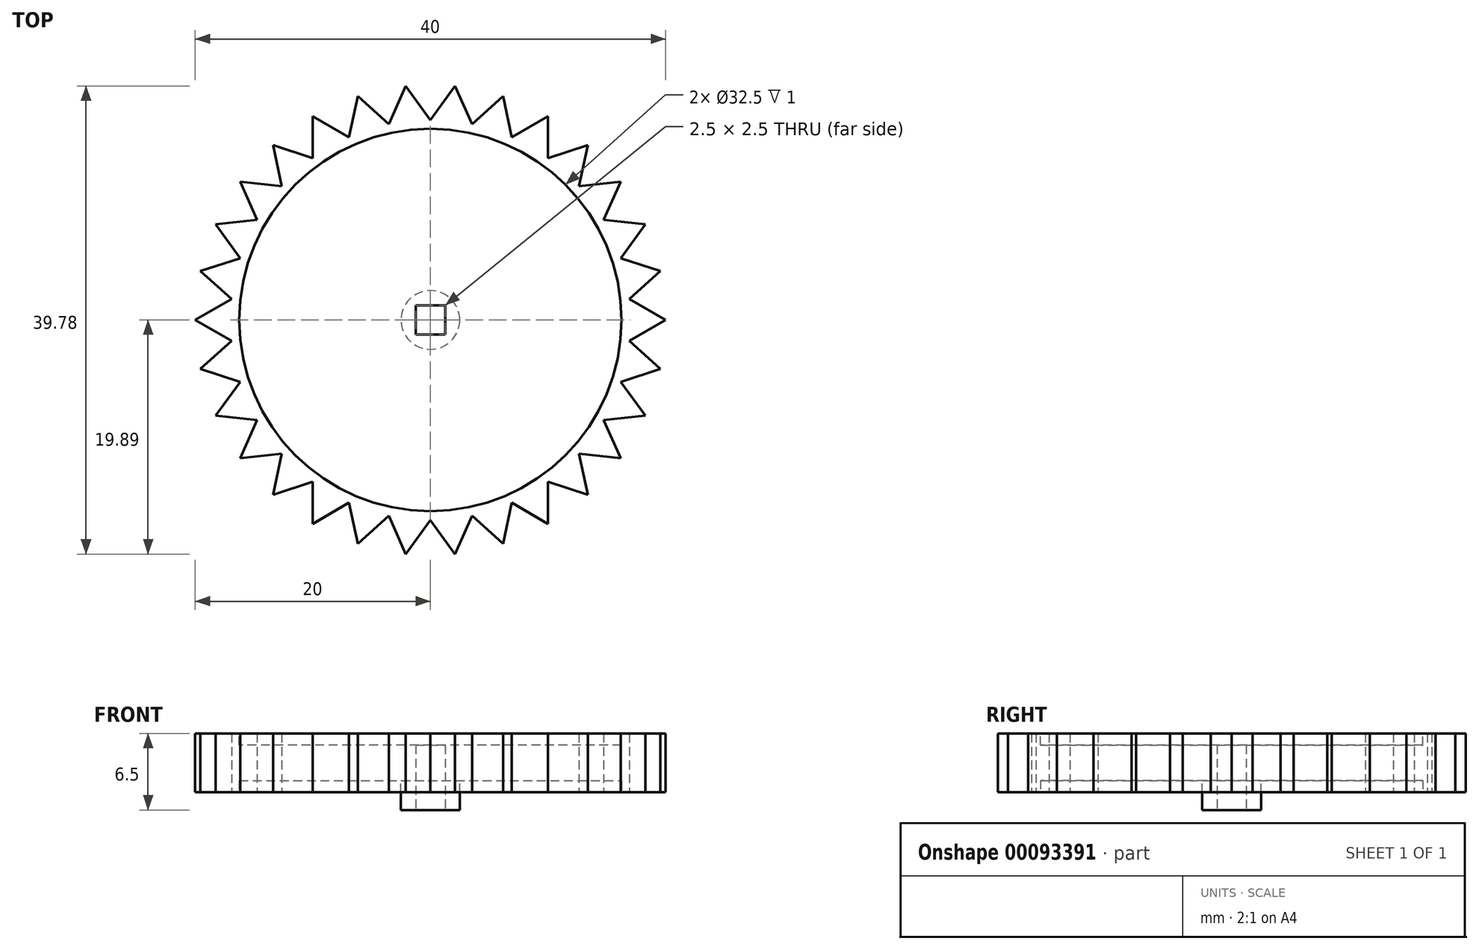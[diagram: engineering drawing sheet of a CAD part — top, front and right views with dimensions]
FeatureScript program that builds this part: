
annotation { "Feature Type Name" : "Feature", "Feature Type Description" : "" }
export const myFeature = defineFeature(function(context is Context, id is Id, definition is map)
    precondition{}
    {
        {
            var Q0;
            Q0=qCreatedBy(makeId("Top.planeOp"),FACE);
            var sketch = newSketch(context, id + "F0", { "sketchPlane" : qUnion([Q0])});
            skCircle(sketch, "E0", {"center": v(0, 0) * mm, "radius": 20 * mm});
            skLineSegment(sketch, "E1", {"start": v(0, 0) * mm, "end": v(-2.1, -19.9) * mm, "construction": true});
            skLineSegment(sketch, "E2", {"start": v(0, 0) * mm, "end": v(2.1, -19.9) * mm, "construction": true});
            skLineSegment(sketch, "E3", {"start": v(-2.1, -19.9) * mm, "end": v(0, -17) * mm});
            skLineSegment(sketch, "E4", {"start": v(0, -17) * mm, "end": v(2.1, -19.9) * mm});
            skArc(sketch, "E5", {"start": v(-2.1, -19.9) * mm, "mid": v(0, -20) * mm, "end": v(2.1, -19.9) * mm});
            skLineSegment(sketch, "E6.1.0", {"start": v(2.1, -19.9) * mm, "end": v(3.54, -16.63) * mm});
            skLineSegment(sketch, "E6.1.1", {"start": v(3.54, -16.63) * mm, "end": v(6.18, -19.02) * mm});
            skArc(sketch, "E6.1.2", {"start": v(2.1, -19.9) * mm, "mid": v(4.16, -19.56) * mm, "end": v(6.18, -19.02) * mm});
            skLineSegment(sketch, "E6.2.0", {"start": v(6.18, -19.02) * mm, "end": v(6.92, -15.53) * mm});
            skLineSegment(sketch, "E6.2.1", {"start": v(6.92, -15.53) * mm, "end": v(10, -17.32) * mm});
            skArc(sketch, "E6.2.2", {"start": v(6.18, -19.02) * mm, "mid": v(8.13, -18.27) * mm, "end": v(10, -17.32) * mm});
            skLineSegment(sketch, "E7.1.3.0", {"start": v(10, -17.32) * mm, "end": v(10, -13.76) * mm});
            skLineSegment(sketch, "E7.3.3.0", {"start": v(10, -13.76) * mm, "end": v(13.38, -14.86) * mm});
            skArc(sketch, "E7.6.3.0", {"start": v(10, -17.32) * mm, "mid": v(11.76, -16.18) * mm, "end": v(13.38, -14.86) * mm});
            skLineSegment(sketch, "E7.1.4.0", {"start": v(13.38, -14.86) * mm, "end": v(12.64, -11.38) * mm});
            skLineSegment(sketch, "E7.3.4.0", {"start": v(12.64, -11.38) * mm, "end": v(16.18, -11.76) * mm});
            skArc(sketch, "E7.6.4.0", {"start": v(13.38, -14.86) * mm, "mid": v(14.86, -13.38) * mm, "end": v(16.18, -11.76) * mm});
            skLineSegment(sketch, "E7.1.5.0", {"start": v(16.18, -11.76) * mm, "end": v(14.73, -8.5) * mm});
            skLineSegment(sketch, "E7.3.5.0", {"start": v(14.73, -8.5) * mm, "end": v(18.27, -8.13) * mm});
            skArc(sketch, "E7.6.5.0", {"start": v(16.18, -11.76) * mm, "mid": v(17.32, -10) * mm, "end": v(18.27, -8.13) * mm});
            skLineSegment(sketch, "E7.1.6.0", {"start": v(18.27, -8.13) * mm, "end": v(16.17, -5.25) * mm});
            skLineSegment(sketch, "E7.3.6.0", {"start": v(16.17, -5.25) * mm, "end": v(19.56, -4.16) * mm});
            skArc(sketch, "E7.6.6.0", {"start": v(18.27, -8.13) * mm, "mid": v(19.02, -6.18) * mm, "end": v(19.56, -4.16) * mm});
            skLineSegment(sketch, "E7.1.7.0", {"start": v(19.56, -4.16) * mm, "end": v(16.91, -1.78) * mm});
            skLineSegment(sketch, "E7.3.7.0", {"start": v(16.91, -1.78) * mm, "end": v(20, 0) * mm});
            skArc(sketch, "E7.6.7.0", {"start": v(19.56, -4.16) * mm, "mid": v(19.9, -2.1) * mm, "end": v(20, 0) * mm});
            skLineSegment(sketch, "E7.1.8.0", {"start": v(20, 0) * mm, "end": v(16.91, 1.78) * mm});
            skLineSegment(sketch, "E7.3.8.0", {"start": v(16.91, 1.78) * mm, "end": v(19.56, 4.16) * mm});
            skArc(sketch, "E7.6.8.0", {"start": v(20, 0) * mm, "mid": v(19.9, 2.1) * mm, "end": v(19.56, 4.16) * mm});
            skLineSegment(sketch, "E7.1.9.0", {"start": v(19.56, 4.16) * mm, "end": v(16.17, 5.25) * mm});
            skLineSegment(sketch, "E7.3.9.0", {"start": v(16.17, 5.25) * mm, "end": v(18.27, 8.13) * mm});
            skArc(sketch, "E7.6.9.0", {"start": v(19.56, 4.16) * mm, "mid": v(19.02, 6.18) * mm, "end": v(18.27, 8.13) * mm});
            skLineSegment(sketch, "E7.1.10.0", {"start": v(18.27, 8.13) * mm, "end": v(14.73, 8.5) * mm});
            skLineSegment(sketch, "E7.3.10.0", {"start": v(14.73, 8.5) * mm, "end": v(16.18, 11.76) * mm});
            skArc(sketch, "E7.6.10.0", {"start": v(18.27, 8.13) * mm, "mid": v(17.32, 10) * mm, "end": v(16.18, 11.76) * mm});
            skLineSegment(sketch, "E7.1.11.0", {"start": v(16.18, 11.76) * mm, "end": v(12.64, 11.38) * mm});
            skLineSegment(sketch, "E7.3.11.0", {"start": v(12.64, 11.38) * mm, "end": v(13.38, 14.86) * mm});
            skArc(sketch, "E7.6.11.0", {"start": v(16.18, 11.76) * mm, "mid": v(14.86, 13.38) * mm, "end": v(13.38, 14.86) * mm});
            skLineSegment(sketch, "E7.1.12.0", {"start": v(13.38, 14.86) * mm, "end": v(10, 13.76) * mm});
            skLineSegment(sketch, "E7.3.12.0", {"start": v(10, 13.76) * mm, "end": v(10, 17.32) * mm});
            skArc(sketch, "E7.6.12.0", {"start": v(13.38, 14.86) * mm, "mid": v(11.76, 16.18) * mm, "end": v(10, 17.32) * mm});
            skLineSegment(sketch, "E7.1.13.0", {"start": v(10, 17.32) * mm, "end": v(6.92, 15.53) * mm});
            skLineSegment(sketch, "E7.3.13.0", {"start": v(6.92, 15.53) * mm, "end": v(6.18, 19.02) * mm});
            skArc(sketch, "E7.6.13.0", {"start": v(10, 17.32) * mm, "mid": v(8.13, 18.27) * mm, "end": v(6.18, 19.02) * mm});
            skLineSegment(sketch, "E7.1.14.0", {"start": v(6.18, 19.02) * mm, "end": v(3.54, 16.63) * mm});
            skLineSegment(sketch, "E7.3.14.0", {"start": v(3.54, 16.63) * mm, "end": v(2.1, 19.9) * mm});
            skArc(sketch, "E7.6.14.0", {"start": v(6.18, 19.02) * mm, "mid": v(4.16, 19.56) * mm, "end": v(2.1, 19.9) * mm});
            skLineSegment(sketch, "E7.1.15.0", {"start": v(2.1, 19.9) * mm, "end": v(0, 17) * mm});
            skLineSegment(sketch, "E7.3.15.0", {"start": v(0, 17) * mm, "end": v(-2.1, 19.9) * mm});
            skArc(sketch, "E7.6.15.0", {"start": v(2.1, 19.9) * mm, "mid": v(0, 20) * mm, "end": v(-2.1, 19.9) * mm});
            skLineSegment(sketch, "E7.1.16.0", {"start": v(-2.1, 19.9) * mm, "end": v(-3.54, 16.63) * mm});
            skLineSegment(sketch, "E7.3.16.0", {"start": v(-3.54, 16.63) * mm, "end": v(-6.18, 19.02) * mm});
            skArc(sketch, "E7.6.16.0", {"start": v(-2.1, 19.9) * mm, "mid": v(-4.16, 19.56) * mm, "end": v(-6.18, 19.02) * mm});
            skLineSegment(sketch, "E7.1.17.0", {"start": v(-6.18, 19.02) * mm, "end": v(-6.92, 15.53) * mm});
            skLineSegment(sketch, "E7.3.17.0", {"start": v(-6.92, 15.53) * mm, "end": v(-10, 17.32) * mm});
            skArc(sketch, "E7.6.17.0", {"start": v(-6.18, 19.02) * mm, "mid": v(-8.13, 18.27) * mm, "end": v(-10, 17.32) * mm});
            skLineSegment(sketch, "E7.1.18.0", {"start": v(-10, 17.32) * mm, "end": v(-10, 13.76) * mm});
            skLineSegment(sketch, "E7.3.18.0", {"start": v(-10, 13.76) * mm, "end": v(-13.38, 14.86) * mm});
            skArc(sketch, "E7.6.18.0", {"start": v(-10, 17.32) * mm, "mid": v(-11.76, 16.18) * mm, "end": v(-13.38, 14.86) * mm});
            skLineSegment(sketch, "E7.1.19.0", {"start": v(-13.38, 14.86) * mm, "end": v(-12.64, 11.38) * mm});
            skLineSegment(sketch, "E7.3.19.0", {"start": v(-12.64, 11.38) * mm, "end": v(-16.18, 11.76) * mm});
            skArc(sketch, "E7.6.19.0", {"start": v(-13.38, 14.86) * mm, "mid": v(-14.86, 13.38) * mm, "end": v(-16.18, 11.76) * mm});
            skLineSegment(sketch, "E7.1.20.0", {"start": v(-16.18, 11.76) * mm, "end": v(-14.73, 8.5) * mm});
            skLineSegment(sketch, "E7.3.20.0", {"start": v(-14.73, 8.5) * mm, "end": v(-18.27, 8.13) * mm});
            skArc(sketch, "E7.6.20.0", {"start": v(-16.18, 11.76) * mm, "mid": v(-17.32, 10) * mm, "end": v(-18.27, 8.13) * mm});
            skLineSegment(sketch, "E7.1.21.0", {"start": v(-18.27, 8.13) * mm, "end": v(-16.17, 5.25) * mm});
            skLineSegment(sketch, "E7.3.21.0", {"start": v(-16.17, 5.25) * mm, "end": v(-19.56, 4.16) * mm});
            skArc(sketch, "E7.6.21.0", {"start": v(-18.27, 8.13) * mm, "mid": v(-19.02, 6.18) * mm, "end": v(-19.56, 4.16) * mm});
            skLineSegment(sketch, "E7.1.22.0", {"start": v(-19.56, 4.16) * mm, "end": v(-16.91, 1.78) * mm});
            skLineSegment(sketch, "E7.3.22.0", {"start": v(-16.91, 1.78) * mm, "end": v(-20, 0) * mm});
            skArc(sketch, "E7.6.22.0", {"start": v(-19.56, 4.16) * mm, "mid": v(-19.9, 2.1) * mm, "end": v(-20, 0) * mm});
            skLineSegment(sketch, "E7.1.23.0", {"start": v(-20, 0) * mm, "end": v(-16.91, -1.78) * mm});
            skLineSegment(sketch, "E7.3.23.0", {"start": v(-16.91, -1.78) * mm, "end": v(-19.56, -4.16) * mm});
            skArc(sketch, "E7.6.23.0", {"start": v(-20, 0) * mm, "mid": v(-19.9, -2.1) * mm, "end": v(-19.56, -4.16) * mm});
            skLineSegment(sketch, "E7.1.24.0", {"start": v(-19.56, -4.16) * mm, "end": v(-16.17, -5.25) * mm});
            skLineSegment(sketch, "E7.3.24.0", {"start": v(-16.17, -5.25) * mm, "end": v(-18.27, -8.13) * mm});
            skArc(sketch, "E7.6.24.0", {"start": v(-19.56, -4.16) * mm, "mid": v(-19.02, -6.18) * mm, "end": v(-18.27, -8.13) * mm});
            skLineSegment(sketch, "E7.1.25.0", {"start": v(-18.27, -8.13) * mm, "end": v(-14.73, -8.5) * mm});
            skLineSegment(sketch, "E7.3.25.0", {"start": v(-14.73, -8.5) * mm, "end": v(-16.18, -11.76) * mm});
            skArc(sketch, "E7.6.25.0", {"start": v(-18.27, -8.13) * mm, "mid": v(-17.32, -10) * mm, "end": v(-16.18, -11.76) * mm});
            skLineSegment(sketch, "E7.1.26.0", {"start": v(-16.18, -11.76) * mm, "end": v(-12.64, -11.38) * mm});
            skLineSegment(sketch, "E7.3.26.0", {"start": v(-12.64, -11.38) * mm, "end": v(-13.38, -14.86) * mm});
            skArc(sketch, "E7.6.26.0", {"start": v(-16.18, -11.76) * mm, "mid": v(-14.86, -13.38) * mm, "end": v(-13.38, -14.86) * mm});
            skLineSegment(sketch, "E7.1.27.0", {"start": v(-13.38, -14.86) * mm, "end": v(-10, -13.76) * mm});
            skLineSegment(sketch, "E7.3.27.0", {"start": v(-10, -13.76) * mm, "end": v(-10, -17.32) * mm});
            skArc(sketch, "E7.6.27.0", {"start": v(-13.38, -14.86) * mm, "mid": v(-11.76, -16.18) * mm, "end": v(-10, -17.32) * mm});
            skLineSegment(sketch, "E7.1.28.0", {"start": v(-10, -17.32) * mm, "end": v(-6.92, -15.53) * mm});
            skLineSegment(sketch, "E7.3.28.0", {"start": v(-6.92, -15.53) * mm, "end": v(-6.18, -19.02) * mm});
            skArc(sketch, "E7.6.28.0", {"start": v(-10, -17.32) * mm, "mid": v(-8.13, -18.27) * mm, "end": v(-6.18, -19.02) * mm});
            skLineSegment(sketch, "E7.1.29.0", {"start": v(-6.18, -19.02) * mm, "end": v(-3.54, -16.63) * mm});
            skLineSegment(sketch, "E7.3.29.0", {"start": v(-3.54, -16.63) * mm, "end": v(-2.1, -19.9) * mm});
            skArc(sketch, "E7.6.29.0", {"start": v(-6.18, -19.02) * mm, "mid": v(-4.16, -19.56) * mm, "end": v(-2.1, -19.9) * mm});
            skLineSegment(sketch, "E8.bottom", {"start": v(-1.25, 1.25) * mm, "end": v(1.25, 1.25) * mm});
            skLineSegment(sketch, "E8.top", {"start": v(-1.25, -1.25) * mm, "end": v(1.25, -1.25) * mm});
            skLineSegment(sketch, "E8.left", {"start": v(-1.25, 1.25) * mm, "end": v(-1.25, -1.25) * mm});
            skLineSegment(sketch, "E8.right", {"start": v(1.25, 1.25) * mm, "end": v(1.25, -1.25) * mm});
            skSolve(sketch);
        }
        {
            var Q0;
            Q0=makeQuery(id+"F0.imprint","IMPRINT",FACE,{"disambiguationData":[TD([[makeQuery(id+"F0.imprint","IMPRINT",EDGE,{"derivedFrom":sQuery(id+"F0.wireOp",EDGE,"E3")}),1.0]])]});
            extrude(context, id + "F1", {"entities" : qUnion([Q0]), "depth" : 5 * mm});
        }
        {
            var Q0;
            Q0=makeQuery(id+"F1.opExtrude","CAP_FACE",FACE,{"disambiguationData":[OSD([sQuery(id+"F0.wireOp",EDGE,"E3"),sQuery(id+"F0.wireOp",EDGE,"E4"),sQuery(id+"F0.wireOp",EDGE,"E6.1.0"),sQuery(id+"F0.wireOp",EDGE,"E6.1.1"),sQuery(id+"F0.wireOp",EDGE,"E6.2.0"),sQuery(id+"F0.wireOp",EDGE,"E6.2.1"),sQuery(id+"F0.wireOp",EDGE,"E7.1.3.0"),sQuery(id+"F0.wireOp",EDGE,"E7.3.3.0"),sQuery(id+"F0.wireOp",EDGE,"E7.1.4.0"),sQuery(id+"F0.wireOp",EDGE,"E7.3.4.0"),sQuery(id+"F0.wireOp",EDGE,"E7.1.5.0"),sQuery(id+"F0.wireOp",EDGE,"E7.3.5.0"),sQuery(id+"F0.wireOp",EDGE,"E7.1.6.0"),sQuery(id+"F0.wireOp",EDGE,"E7.3.6.0"),sQuery(id+"F0.wireOp",EDGE,"E7.1.7.0"),sQuery(id+"F0.wireOp",EDGE,"E7.3.7.0"),sQuery(id+"F0.wireOp",EDGE,"E7.1.8.0"),sQuery(id+"F0.wireOp",EDGE,"E7.3.8.0"),sQuery(id+"F0.wireOp",EDGE,"E7.1.9.0"),sQuery(id+"F0.wireOp",EDGE,"E7.3.9.0"),sQuery(id+"F0.wireOp",EDGE,"E7.1.10.0"),sQuery(id+"F0.wireOp",EDGE,"E7.3.10.0"),sQuery(id+"F0.wireOp",EDGE,"E7.1.11.0"),sQuery(id+"F0.wireOp",EDGE,"E7.3.11.0"),sQuery(id+"F0.wireOp",EDGE,"E7.1.12.0"),sQuery(id+"F0.wireOp",EDGE,"E7.3.12.0"),sQuery(id+"F0.wireOp",EDGE,"E7.1.13.0"),sQuery(id+"F0.wireOp",EDGE,"E7.3.13.0"),sQuery(id+"F0.wireOp",EDGE,"E7.1.14.0"),sQuery(id+"F0.wireOp",EDGE,"E7.3.14.0"),sQuery(id+"F0.wireOp",EDGE,"E7.1.15.0"),sQuery(id+"F0.wireOp",EDGE,"E7.3.15.0"),sQuery(id+"F0.wireOp",EDGE,"E7.1.16.0"),sQuery(id+"F0.wireOp",EDGE,"E7.3.16.0"),sQuery(id+"F0.wireOp",EDGE,"E7.1.17.0"),sQuery(id+"F0.wireOp",EDGE,"E7.3.17.0"),sQuery(id+"F0.wireOp",EDGE,"E7.1.18.0"),sQuery(id+"F0.wireOp",EDGE,"E7.3.18.0"),sQuery(id+"F0.wireOp",EDGE,"E7.1.19.0"),sQuery(id+"F0.wireOp",EDGE,"E7.3.19.0"),sQuery(id+"F0.wireOp",EDGE,"E7.1.20.0"),sQuery(id+"F0.wireOp",EDGE,"E7.3.20.0"),sQuery(id+"F0.wireOp",EDGE,"E7.1.21.0"),sQuery(id+"F0.wireOp",EDGE,"E7.3.21.0"),sQuery(id+"F0.wireOp",EDGE,"E7.1.22.0"),sQuery(id+"F0.wireOp",EDGE,"E7.3.22.0"),sQuery(id+"F0.wireOp",EDGE,"E7.1.23.0"),sQuery(id+"F0.wireOp",EDGE,"E7.3.23.0"),sQuery(id+"F0.wireOp",EDGE,"E7.1.24.0"),sQuery(id+"F0.wireOp",EDGE,"E7.3.24.0"),sQuery(id+"F0.wireOp",EDGE,"E7.1.25.0"),sQuery(id+"F0.wireOp",EDGE,"E7.3.25.0"),sQuery(id+"F0.wireOp",EDGE,"E7.1.26.0"),sQuery(id+"F0.wireOp",EDGE,"E7.3.26.0"),sQuery(id+"F0.wireOp",EDGE,"E7.1.27.0"),sQuery(id+"F0.wireOp",EDGE,"E7.3.27.0"),sQuery(id+"F0.wireOp",EDGE,"E7.1.28.0"),sQuery(id+"F0.wireOp",EDGE,"E7.3.28.0"),sQuery(id+"F0.wireOp",EDGE,"E7.1.29.0"),sQuery(id+"F0.wireOp",EDGE,"E7.3.29.0"),sQuery(id+"F0.wireOp",EDGE,"E8.bottom"),sQuery(id+"F0.wireOp",EDGE,"E8.top"),sQuery(id+"F0.wireOp",EDGE,"E8.left"),sQuery(id+"F0.wireOp",EDGE,"E8.right")])],"isStart":true});
            var sketch = newSketch(context, id + "F2", { "sketchPlane" : qUnion([Q0])});
            skCircle(sketch, "E9", {"center": v(0, 0) * mm, "radius": 16.25 * mm});
            skSolve(sketch);
        }
        {
            var Q0;
            Q0=makeQuery(id+"F2.imprint","IMPRINT",FACE,{"disambiguationData":[TD([[makeQuery(id+"F2.imprint","IMPRINT",EDGE,{"derivedFrom":sQuery(id+"F2.wireOp",EDGE,"E9")}),1.0]])]});
            extrude(context, id + "F3", {"entities" : qUnion([Q0]), "operationType" : NewBodyOperationType.REMOVE, "oppositeDirection" : true, "depth" : 1 * mm});
        }
        {
            var Q0;
            Q0=makeQuery(id+"F1.opExtrude","CAP_FACE",FACE,{"disambiguationData":[OSD([sQuery(id+"F0.wireOp",EDGE,"E3"),sQuery(id+"F0.wireOp",EDGE,"E4"),sQuery(id+"F0.wireOp",EDGE,"E6.1.0"),sQuery(id+"F0.wireOp",EDGE,"E6.1.1"),sQuery(id+"F0.wireOp",EDGE,"E6.2.0"),sQuery(id+"F0.wireOp",EDGE,"E6.2.1"),sQuery(id+"F0.wireOp",EDGE,"E7.1.3.0"),sQuery(id+"F0.wireOp",EDGE,"E7.3.3.0"),sQuery(id+"F0.wireOp",EDGE,"E7.1.4.0"),sQuery(id+"F0.wireOp",EDGE,"E7.3.4.0"),sQuery(id+"F0.wireOp",EDGE,"E7.1.5.0"),sQuery(id+"F0.wireOp",EDGE,"E7.3.5.0"),sQuery(id+"F0.wireOp",EDGE,"E7.1.6.0"),sQuery(id+"F0.wireOp",EDGE,"E7.3.6.0"),sQuery(id+"F0.wireOp",EDGE,"E7.1.7.0"),sQuery(id+"F0.wireOp",EDGE,"E7.3.7.0"),sQuery(id+"F0.wireOp",EDGE,"E7.1.8.0"),sQuery(id+"F0.wireOp",EDGE,"E7.3.8.0"),sQuery(id+"F0.wireOp",EDGE,"E7.1.9.0"),sQuery(id+"F0.wireOp",EDGE,"E7.3.9.0"),sQuery(id+"F0.wireOp",EDGE,"E7.1.10.0"),sQuery(id+"F0.wireOp",EDGE,"E7.3.10.0"),sQuery(id+"F0.wireOp",EDGE,"E7.1.11.0"),sQuery(id+"F0.wireOp",EDGE,"E7.3.11.0"),sQuery(id+"F0.wireOp",EDGE,"E7.1.12.0"),sQuery(id+"F0.wireOp",EDGE,"E7.3.12.0"),sQuery(id+"F0.wireOp",EDGE,"E7.1.13.0"),sQuery(id+"F0.wireOp",EDGE,"E7.3.13.0"),sQuery(id+"F0.wireOp",EDGE,"E7.1.14.0"),sQuery(id+"F0.wireOp",EDGE,"E7.3.14.0"),sQuery(id+"F0.wireOp",EDGE,"E7.1.15.0"),sQuery(id+"F0.wireOp",EDGE,"E7.3.15.0"),sQuery(id+"F0.wireOp",EDGE,"E7.1.16.0"),sQuery(id+"F0.wireOp",EDGE,"E7.3.16.0"),sQuery(id+"F0.wireOp",EDGE,"E7.1.17.0"),sQuery(id+"F0.wireOp",EDGE,"E7.3.17.0"),sQuery(id+"F0.wireOp",EDGE,"E7.1.18.0"),sQuery(id+"F0.wireOp",EDGE,"E7.3.18.0"),sQuery(id+"F0.wireOp",EDGE,"E7.1.19.0"),sQuery(id+"F0.wireOp",EDGE,"E7.3.19.0"),sQuery(id+"F0.wireOp",EDGE,"E7.1.20.0"),sQuery(id+"F0.wireOp",EDGE,"E7.3.20.0"),sQuery(id+"F0.wireOp",EDGE,"E7.1.21.0"),sQuery(id+"F0.wireOp",EDGE,"E7.3.21.0"),sQuery(id+"F0.wireOp",EDGE,"E7.1.22.0"),sQuery(id+"F0.wireOp",EDGE,"E7.3.22.0"),sQuery(id+"F0.wireOp",EDGE,"E7.1.23.0"),sQuery(id+"F0.wireOp",EDGE,"E7.3.23.0"),sQuery(id+"F0.wireOp",EDGE,"E7.1.24.0"),sQuery(id+"F0.wireOp",EDGE,"E7.3.24.0"),sQuery(id+"F0.wireOp",EDGE,"E7.1.25.0"),sQuery(id+"F0.wireOp",EDGE,"E7.3.25.0"),sQuery(id+"F0.wireOp",EDGE,"E7.1.26.0"),sQuery(id+"F0.wireOp",EDGE,"E7.3.26.0"),sQuery(id+"F0.wireOp",EDGE,"E7.1.27.0"),sQuery(id+"F0.wireOp",EDGE,"E7.3.27.0"),sQuery(id+"F0.wireOp",EDGE,"E7.1.28.0"),sQuery(id+"F0.wireOp",EDGE,"E7.3.28.0"),sQuery(id+"F0.wireOp",EDGE,"E7.1.29.0"),sQuery(id+"F0.wireOp",EDGE,"E7.3.29.0"),sQuery(id+"F0.wireOp",EDGE,"E8.bottom"),sQuery(id+"F0.wireOp",EDGE,"E8.top"),sQuery(id+"F0.wireOp",EDGE,"E8.left"),sQuery(id+"F0.wireOp",EDGE,"E8.right")])],"isStart":false});
            var sketch = newSketch(context, id + "F4", { "sketchPlane" : qUnion([Q0])});
            skCircle(sketch, "E10", {"center": v(0, 0) * mm, "radius": 16.25 * mm});
            skSolve(sketch);
        }
        {
            var Q0;
            Q0=makeQuery(id+"F4.imprint","IMPRINT",FACE,{"disambiguationData":[TD([[makeQuery(id+"F4.imprint","IMPRINT",EDGE,{"derivedFrom":sQuery(id+"F4.wireOp",EDGE,"E10")}),1.0]])]});
            extrude(context, id + "F5", {"entities" : qUnion([Q0]), "operationType" : NewBodyOperationType.REMOVE, "oppositeDirection" : true, "depth" : 1 * mm});
        }
        {
            var Q0;
            Q0=makeQuery(id+"F3.boolean.opBoolean","COPY",FACE,{"derivedFrom":makeQuery(id+"F3.opExtrude","CAP_FACE",FACE,{"disambiguationData":[OSD([sQuery(id+"F0.wireOp",EDGE,"E8.bottom"),sQuery(id+"F0.wireOp",EDGE,"E8.top"),sQuery(id+"F0.wireOp",EDGE,"E8.left"),sQuery(id+"F0.wireOp",EDGE,"E8.right"),sQuery(id+"F2.wireOp",EDGE,"E9")])],"isStart":false})});
            var sketch = newSketch(context, id + "F6", { "sketchPlane" : qUnion([Q0])});
            skCircle(sketch, "E11", {"center": v(0, 0) * mm, "radius": 2.5 * mm});
            skSolve(sketch);
        }
        {
            var Q0;
            Q0=makeQuery(id+"F6.imprint","IMPRINT",FACE,{"disambiguationData":[TD([[makeQuery(id+"F6.imprint","IMPRINT",EDGE,{"derivedFrom":sQuery(id+"F6.wireOp",EDGE,"E11")}),1.0]])]});
            extrude(context, id + "F7", {"entities" : qUnion([Q0]), "operationType" : NewBodyOperationType.ADD, "depth" : 2.5 * mm});
        }
    });
